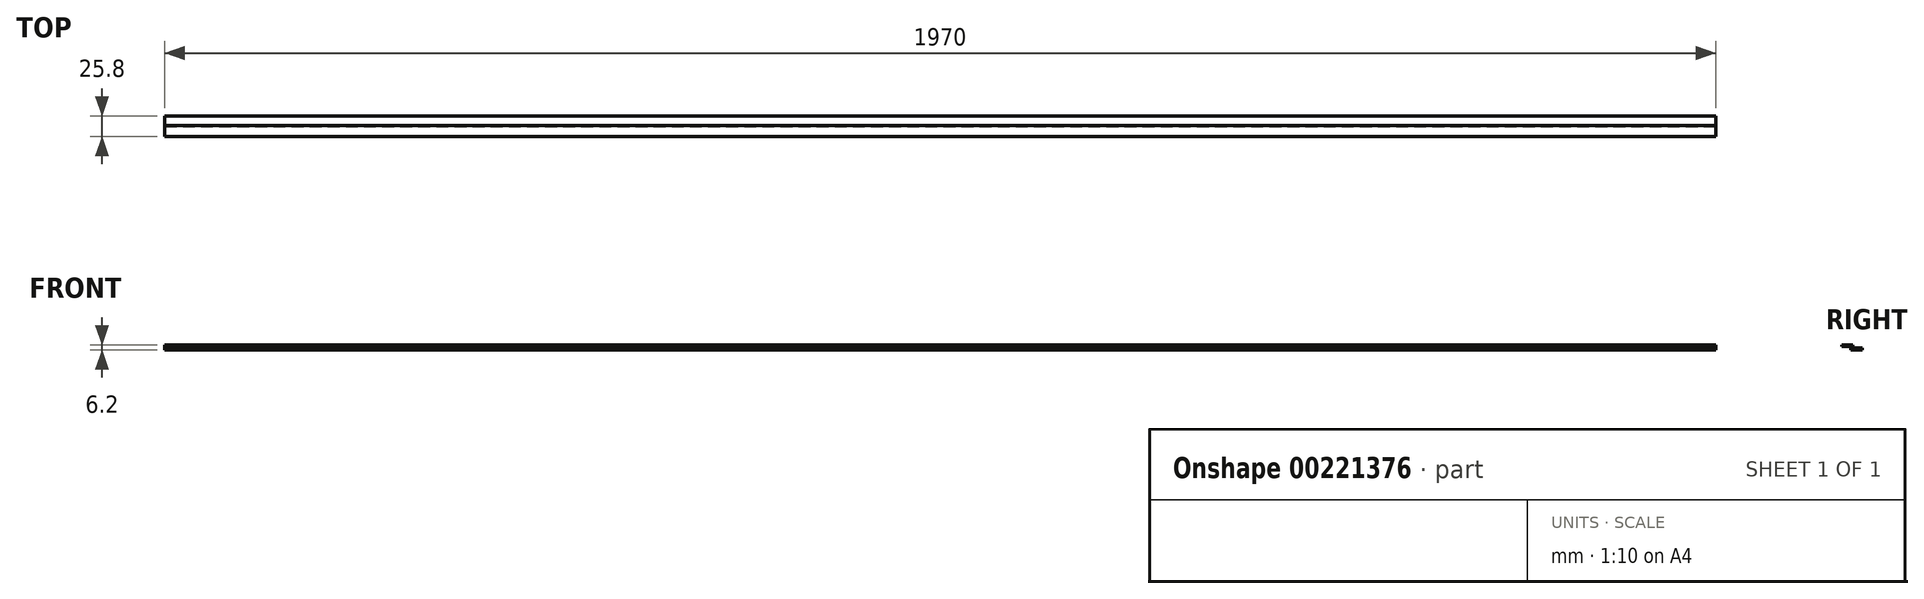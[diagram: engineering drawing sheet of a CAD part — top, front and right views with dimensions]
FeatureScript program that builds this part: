
annotation { "Feature Type Name" : "Feature", "Feature Type Description" : "" }
export const myFeature = defineFeature(function(context is Context, id is Id, definition is map)
    precondition{}
    {
        {
            var Q0;
            Q0=qCreatedBy(makeId("Right.planeOp"),FACE);
            var sketch = newSketch(context, id + "F0", { "sketchPlane" : qUnion([Q0])});
            skLineSegment(sketch, "E0", {"start": v(0, 0) * mm, "end": v(0, -4) * mm});
            skLineSegment(sketch, "E1", {"start": v(0, -4) * mm, "end": v(11.8, -4) * mm});
            skLineSegment(sketch, "E2", {"start": v(11.8, -4) * mm, "end": v(11.8, -6.2) * mm});
            skLineSegment(sketch, "E3", {"start": v(11.8, -6.2) * mm, "end": v(-2.2, -6.2) * mm});
            skLineSegment(sketch, "E4", {"start": v(-2.2, -6.2) * mm, "end": v(-2.2, -2.2) * mm});
            skLineSegment(sketch, "E5", {"start": v(-2.2, -2.2) * mm, "end": v(-14, -2.2) * mm});
            skLineSegment(sketch, "E6", {"start": v(-14, -2.2) * mm, "end": v(-14, 0) * mm});
            skLineSegment(sketch, "E7", {"start": v(-14, 0) * mm, "end": v(0, 0) * mm});
            skSolve(sketch);
        }
        {
            var Q0;
            Q0=qSketchRegion(id+"F0",true);
            extrude(context, id + "F1", {"entities" : qUnion([Q0]), "depth" : 1970 * mm, "symmetric" : true});
        }
    });
